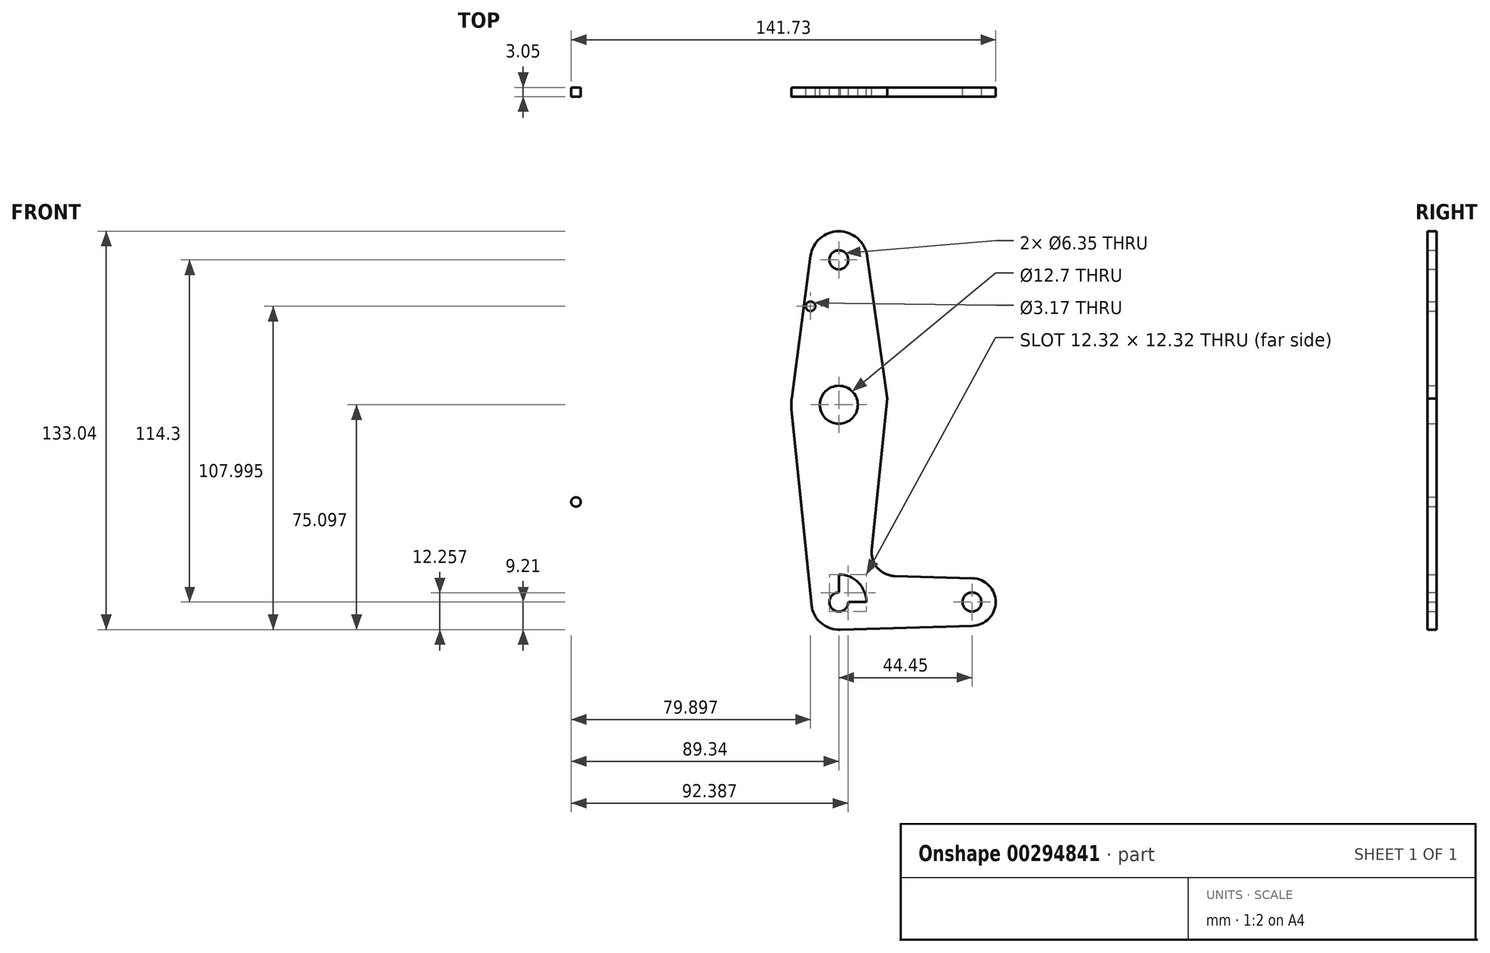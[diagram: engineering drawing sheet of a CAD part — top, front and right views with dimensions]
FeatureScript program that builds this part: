
annotation { "Feature Type Name" : "Feature", "Feature Type Description" : "" }
export const myFeature = defineFeature(function(context is Context, id is Id, definition is map)
    precondition{}
    {
        {
            var Q0;
            Q0=qCreatedBy(makeId("Front.planeOp"),FACE);
            var sketch = newSketch(context, id + "F0", { "sketchPlane" : qUnion([Q0])});
            skCircle(sketch, "E0", {"center": v(0, 0) * mm, "radius": 9.2 * mm});
            skCircle(sketch, "E1", {"center": v(0, 65.89) * mm, "radius": 15.88 * mm});
            skCircle(sketch, "E2", {"center": v(0, 114.3) * mm, "radius": 9.53 * mm});
            skCircle(sketch, "E3", {"center": v(44.45, 0) * mm, "radius": 7.94 * mm});
            skLineSegment(sketch, "E4", {"start": v(0, 114.3) * mm, "end": v(0, 0) * mm});
            skLineSegment(sketch, "E5", {"start": v(0, 0) * mm, "end": v(44.45, 0) * mm});
            skLineSegment(sketch, "E6", {"start": v(-9.44, 115.55) * mm, "end": v(-15.74, 67.97) * mm});
            skLineSegment(sketch, "E7", {"start": v(0, -9.2) * mm, "end": v(44.68, -7.93) * mm});
            skLineSegment(sketch, "E8", {"start": v(44.68, 7.93) * mm, "end": v(18.68, 8.68) * mm});
            skLineSegment(sketch, "E9", {"start": v(11, 17.43) * mm, "end": v(16.17, 67.97) * mm});
            skLineSegment(sketch, "E10", {"start": v(16.17, 67.97) * mm, "end": v(9.43, 115.63) * mm});
            skLineSegment(sketch, "E11", {"start": v(-11.82, 97.57) * mm, "end": v(-9.44, 98.79) * mm});
            skCircle(sketch, "E12", {"center": v(-87.75, 33.43) * mm, "radius": 1.59 * mm});
            skCircle(sketch, "E13", {"center": v(-9.44, 98.79) * mm, "radius": 1.59 * mm});
            skCircle(sketch, "E14", {"center": v(0, 114.3) * mm, "radius": 3.18 * mm});
            skCircle(sketch, "E15", {"center": v(0, 65.89) * mm, "radius": 6.35 * mm});
            skCircle(sketch, "E16", {"center": v(0, 0) * mm, "radius": 3.18 * mm});
            skCircle(sketch, "E17", {"center": v(44.45, 0) * mm, "radius": 3.18 * mm});
            skPoint(sketch, "E18.newPointA", {"position": v(0, 9.21) * mm});
            skArc(sketch, "E18.filletArc", {"start": v(11, 17.43) * mm, "mid": v(12.93, 11.38) * mm, "end": v(18.68, 8.68) * mm});
            skLineSegment(sketch, "E19", {"start": v(-15.8, 64.28) * mm, "end": v(-9.16, -0.93) * mm});
            skSolve(sketch);
        }
        {
            var Q0;
            Q0 = qSketchRegion(id + "F0", true);
            extrude(context, id + "F1", {"entities" : qUnion([Q0]), "depth" : 3.05 * mm});
        }
    });
